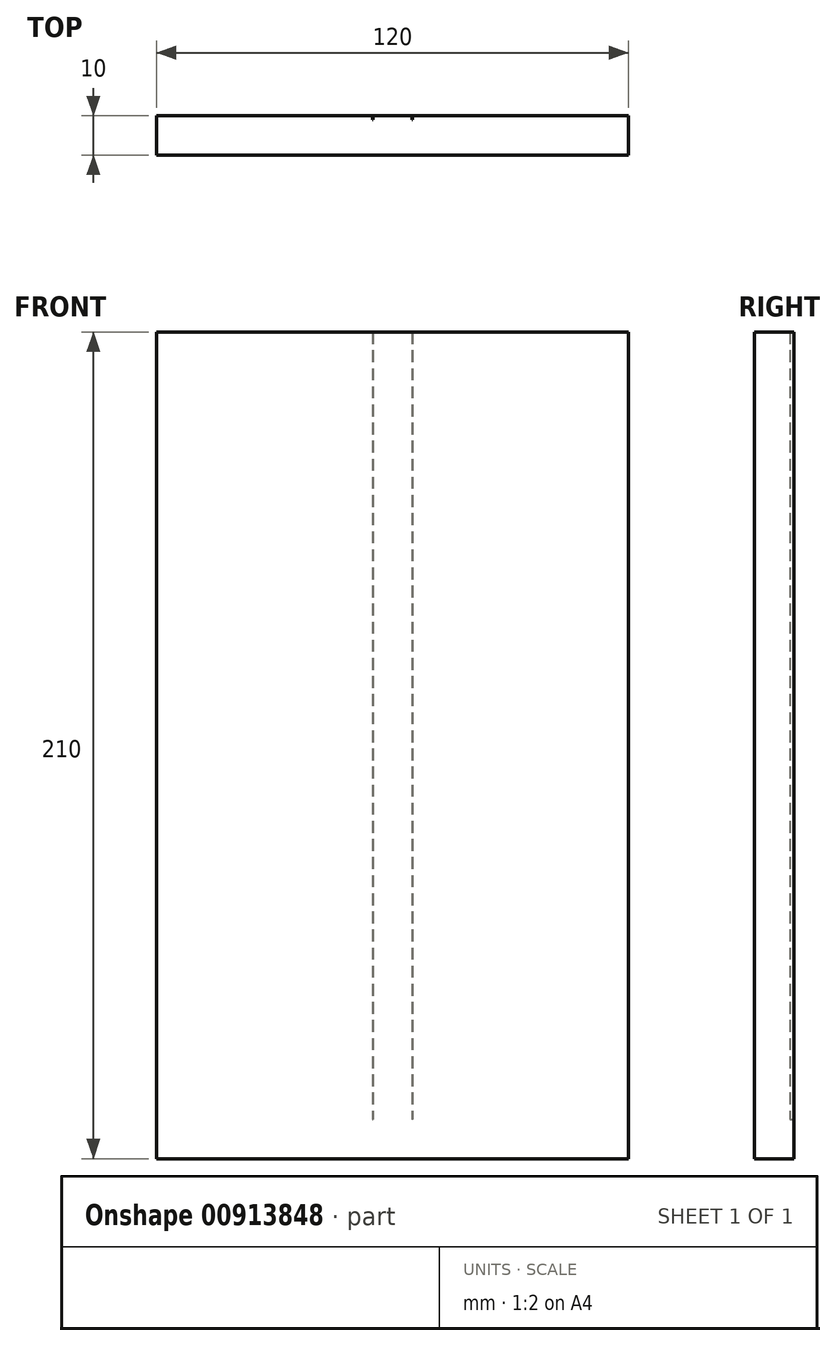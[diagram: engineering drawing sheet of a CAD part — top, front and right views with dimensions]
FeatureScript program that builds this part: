
annotation { "Feature Type Name" : "Feature", "Feature Type Description" : "" }
export const myFeature = defineFeature(function(context is Context, id is Id, definition is map)
    precondition{}
    {
        {
            var Q0;
            Q0=qCreatedBy(makeId("Front.planeOp"),FACE);
            var sketch = newSketch(context, id + "F0", { "sketchPlane" : qUnion([Q0])});
            skLineSegment(sketch, "E0.bottom", {"start": v(0, 0) * mm, "end": v(-120, 0) * mm});
            skLineSegment(sketch, "E0.top", {"start": v(0, 210) * mm, "end": v(-120, 210) * mm});
            skLineSegment(sketch, "E0.left", {"start": v(0, 0) * mm, "end": v(0, 210) * mm});
            skLineSegment(sketch, "E0.right", {"start": v(-120, 0) * mm, "end": v(-120, 210) * mm});
            skSolve(sketch);
        }
        {
            var Q0;
            Q0=makeQuery(id+"F0.imprint","IMPRINT",FACE,{"disambiguationData":[TD([[makeQuery(id+"F0.imprint","IMPRINT",EDGE,{"derivedFrom":sQuery(id+"F0.wireOp",EDGE,"E0.bottom")}),-1.0]])]});
            extrude(context, id + "F1", {"entities" : qUnion([Q0]), "depth" : 10 * mm, "offsetDistance" : 25 * mm});
        }
        {
            var Q0;
            Q0=makeQuery(id+"F1.opExtrude","CAP_FACE",FACE,{"disambiguationData":[OSD([sQuery(id+"F0.wireOp",EDGE,"E0.bottom"),sQuery(id+"F0.wireOp",EDGE,"E0.top"),sQuery(id+"F0.wireOp",EDGE,"E0.left"),sQuery(id+"F0.wireOp",EDGE,"E0.right")])],"isStart":true});
            var sketch = newSketch(context, id + "F2", { "sketchPlane" : qUnion([Q0])});
            skLineSegment(sketch, "E1", {"start": v(60, 210) * mm, "end": v(60, 0) * mm, "construction": true});
            skLineSegment(sketch, "E2", {"start": v(55, 210) * mm, "end": v(55, 0) * mm, "construction": true});
            skLineSegment(sketch, "E3.bottom", {"start": v(54.95, 210) * mm, "end": v(55.05, 210) * mm});
            skLineSegment(sketch, "E3.top", {"start": v(54.95, 10) * mm, "end": v(55.05, 10) * mm});
            skLineSegment(sketch, "E3.left", {"start": v(54.95, 210) * mm, "end": v(54.95, 10) * mm});
            skLineSegment(sketch, "E3.right", {"start": v(55.05, 210) * mm, "end": v(55.05, 10) * mm});
            skLineSegment(sketch, "E4.MirrorCS", {"start": v(65.05, 210) * mm, "end": v(65.05, 10) * mm});
            skLineSegment(sketch, "E5.MirrorCS", {"start": v(64.95, 210) * mm, "end": v(64.95, 10) * mm});
            skLineSegment(sketch, "E6.MirrorCS", {"start": v(65.05, 10) * mm, "end": v(64.95, 10) * mm});
            skLineSegment(sketch, "E7.MirrorCS", {"start": v(65.05, 210) * mm, "end": v(64.95, 210) * mm});
            skSolve(sketch);
        }
        {
            var Q0;
            Q0 = qSketchRegion(id + "F2", true);
            extrude(context, id + "F3", {"entities" : qUnion([Q0]), "operationType" : NewBodyOperationType.REMOVE, "oppositeDirection" : true, "depth" : 1 * mm, "offsetDistance" : 25 * mm});
        }
    });
